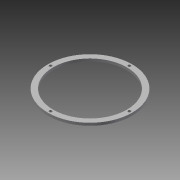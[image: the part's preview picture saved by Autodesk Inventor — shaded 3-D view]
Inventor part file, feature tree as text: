
AUTODESK INVENTOR PART (.ipt)
format: ipt  version: 2013 (Build 170138000, 138)  size: 88,064 bytes
history: native  units: in
note: dims shown in document units (in); Inventor stores cm internally (conversion verified against a paired STEP export)
features: extrude x1, sketch x1
ambient origin geometry x8: Origin, YZ Plane, XZ Plane, XY Plane, X Axis, Y Axis, Z Axis, Center Point
bodies: Solid1 (feature_tree)
feature tree (2):
  extrude  "Extrusion1"  Depth=8.0in
  sketch  "Sketch1"  dims[d0=7.0in d1=8.0in d2=7.5in d3=0.266in d4=1.5748in d6=360.0deg d8=0.25in d9=0.0in]
